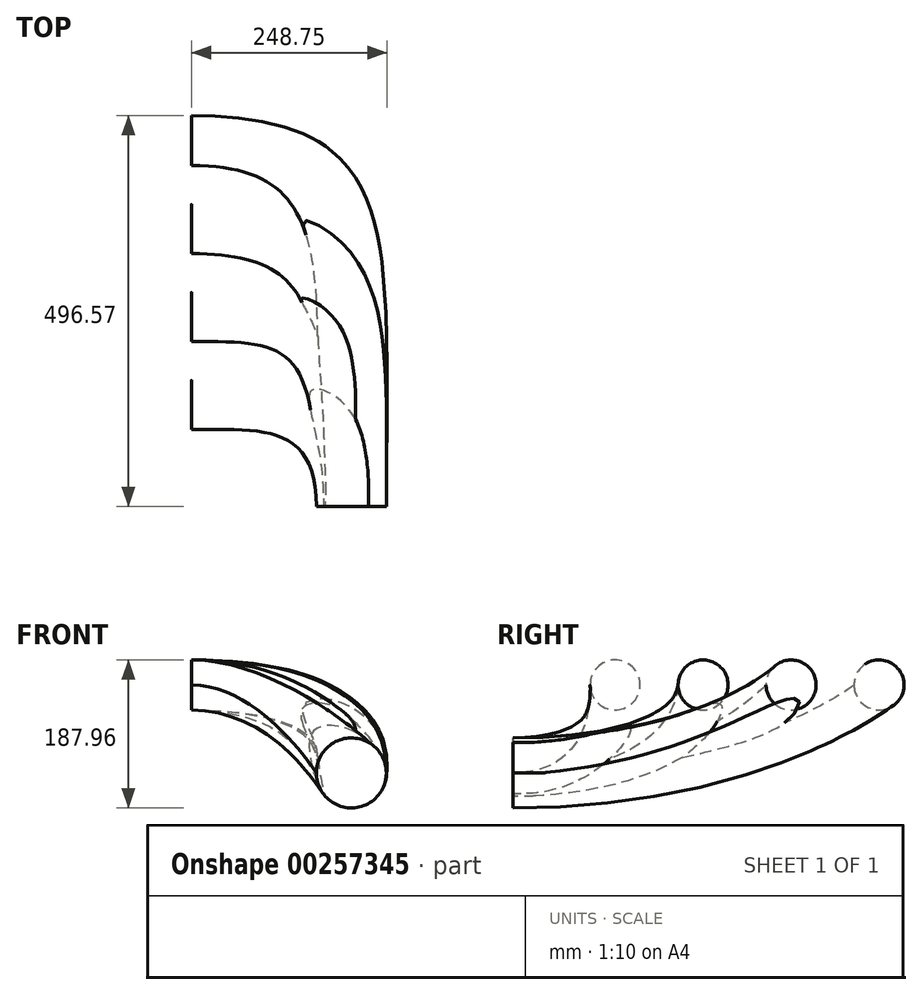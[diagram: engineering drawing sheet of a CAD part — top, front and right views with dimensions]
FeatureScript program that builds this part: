
annotation { "Feature Type Name" : "Feature", "Feature Type Description" : "" }
export const myFeature = defineFeature(function(context is Context, id is Id, definition is map)
    precondition{}
    {
        {
            var Q0;
            Q0=qCreatedBy(makeId("Right.planeOp"),FACE);
            cPlane(context, id + "F0", {"entities" : qUnion([Q0]), "cplaneType" : CPlaneType.OFFSET, "offset" : 203.2 * mm, "oppositeDirection" : true, "width" : 152.4 * mm, "height" : 152.4 * mm});
        }
        {
            var Q0;
            Q0=qCreatedBy(makeId("Top.planeOp"),FACE);
            cPlane(context, id + "F1", {"entities" : qUnion([Q0]), "cplaneType" : CPlaneType.OFFSET, "offset" : 111.76 * mm, "width" : 152.4 * mm, "height" : 152.4 * mm});
        }
        {
            var Q0;
            Q0=qCreatedBy(makeId("Front.planeOp"),FACE);
            var sketch = newSketch(context, id + "F2", { "sketchPlane" : qUnion([Q0])});
            skCircle(sketch, "E0", {"center": v(0, 0) * mm, "radius": 44.45 * mm});
            skSolve(sketch);
        }
        {
            var Q0;
            Q0=qCreatedBy(id+"F0.planeOp",FACE);
            var sketch = newSketch(context, id + "F3", { "sketchPlane" : qUnion([Q0])});
            skCircle(sketch, "E1", {"center": v(129.54, 111.76) * mm, "radius": 31.75 * mm});
            skCircle(sketch, "E2.1.0.0", {"center": v(241.3, 111.76) * mm, "radius": 31.75 * mm});
            skCircle(sketch, "E2.2.0.0", {"center": v(353.06, 111.76) * mm, "radius": 31.75 * mm});
            skCircle(sketch, "E2.3.0.0", {"center": v(464.82, 111.76) * mm, "radius": 31.75 * mm});
            skLineSegment(sketch, "E2.direction1", {"start": v(129.54, 111.76) * mm, "end": v(241.3, 111.76) * mm, "construction": true});
            skSolve(sketch);
        }
        {
            var Q0;
            Q0=qCreatedBy(id+"F1.planeOp",FACE);
            var sketch = newSketch(context, id + "F4", { "sketchPlane" : qUnion([Q0])});
            skLineSegment(sketch, "E3.0", {"start": v(-203.2, 161.3) * mm, "end": v(-203.2, 97.8) * mm, "construction": true});
            skLineSegment(sketch, "E4.0", {"start": v(-203.2, 273.05) * mm, "end": v(-203.2, 209.55) * mm, "construction": true});
            skLineSegment(sketch, "E5.0", {"start": v(-203.2, 384.81) * mm, "end": v(-203.2, 321.31) * mm, "construction": true});
            skLineSegment(sketch, "E6.0", {"start": v(-203.2, 496.57) * mm, "end": v(-203.2, 433.07) * mm, "construction": true});
            skLineSegment(sketch, "E7", {"start": v(-203.2, 97.8) * mm, "end": v(-177.8, 97.8) * mm, "construction": true});
            skLineSegment(sketch, "E8", {"start": v(-203.2, 209.55) * mm, "end": v(-177.8, 209.55) * mm, "construction": true});
            skLineSegment(sketch, "E9", {"start": v(-203.2, 321.31) * mm, "end": v(-177.8, 321.31) * mm, "construction": true});
            skLineSegment(sketch, "E10", {"start": v(-203.2, 433.07) * mm, "end": v(-177.8, 433.07) * mm, "construction": true});
            skSolve(sketch);
        }
        {
            var Q0;
            Q0=qCreatedBy(makeId("Top.planeOp"),FACE);
            var sketch = newSketch(context, id + "F5", { "sketchPlane" : qUnion([Q0])});
            skLineSegment(sketch, "E11.0", {"start": v(44.45, 0) * mm, "end": v(-44.45, 0) * mm, "construction": true});
            skLineSegment(sketch, "E12", {"start": v(-44.45, 0) * mm, "end": v(-44.45, 25.4) * mm, "construction": true});
            skSolve(sketch);
        }
        {
            var Q0;
            Q0=makeQuery(id+"F3.imprint","IMPRINT",FACE,{"disambiguationData":[TD([[makeQuery(id+"F3.imprint","IMPRINT",EDGE,{"derivedFrom":sQuery(id+"F3.wireOp",EDGE,"E1")}),1.0]])]});
            var Q1;
            Q1=makeQuery(id+"F2.imprint","IMPRINT",FACE,{"disambiguationData":[TD([[makeQuery(id+"F2.imprint","IMPRINT",EDGE,{"derivedFrom":sQuery(id+"F2.wireOp",EDGE,"E0")}),1.0]])]});
            var Q2;
            Q2=sQuery(id+"F4.wireOp",VERTEX,"E3.0.end");
            var Q3;
            Q3=sQuery(id+"F5.wireOp",VERTEX,"E12.start");
            loft(context, id + "F6", {"startCondition" : LoftEndDerivativeType.NORMAL_TO_PROFILE, "startMagnitude" : 1.6, "endCondition" : LoftEndDerivativeType.NORMAL_TO_PROFILE, "endMagnitude" : 2.9, "sheetProfilesArray" : [{ "sheetProfileEntities" : qUnion([Q0]) }, { "sheetProfileEntities" : qUnion([Q1]) }], "matchConnections" : true, "connections" : [{ "connectionEntities" : qUnion([Q2, Q3]), "connectionEdgeQueries" : qUnion([]), "connectionEdgeParameters" : [] }]});
        }
        {
            var Q1;
            Q1=makeQuery(id+"F3.imprint","IMPRINT",FACE,{"disambiguationData":[TD([[makeQuery(id+"F3.imprint","IMPRINT",EDGE,{"derivedFrom":sQuery(id+"F3.wireOp",EDGE,"E2.1.0.0")}),1.0]])]});
            var Q2;
            Q2=makeQuery(id+"F2.imprint","IMPRINT",FACE,{"disambiguationData":[TD([[makeQuery(id+"F2.imprint","IMPRINT",EDGE,{"derivedFrom":sQuery(id+"F2.wireOp",EDGE,"E0")}),1.0]])]});
            var Q3;
            Q3=sQuery(id+"F4.wireOp",VERTEX,"E8.start");
            var Q4;
            Q4=sQuery(id+"F5.wireOp",VERTEX,"E12.start");
            loft(context, id + "F7", {"operationType" : NewBodyOperationType.ADD, "startCondition" : LoftEndDerivativeType.NORMAL_TO_PROFILE, "startMagnitude" : 2.2, "endCondition" : LoftEndDerivativeType.NORMAL_TO_PROFILE, "endMagnitude" : 2.9, "sheetProfilesArray" : [{ "sheetProfileEntities" : qUnion([Q1]) }, { "sheetProfileEntities" : qUnion([Q2]) }], "matchConnections" : true, "connections" : [{ "connectionEntities" : qUnion([Q3, Q4]), "connectionEdgeQueries" : qUnion([]), "connectionEdgeParameters" : [] }]});
        }
        {
            var Q1;
            Q1=makeQuery(id+"F3.imprint","IMPRINT",FACE,{"disambiguationData":[TD([[makeQuery(id+"F3.imprint","IMPRINT",EDGE,{"derivedFrom":sQuery(id+"F3.wireOp",EDGE,"E2.2.0.0")}),1.0]])]});
            var Q2;
            Q2=makeQuery(id+"F2.imprint","IMPRINT",FACE,{"disambiguationData":[TD([[makeQuery(id+"F2.imprint","IMPRINT",EDGE,{"derivedFrom":sQuery(id+"F2.wireOp",EDGE,"E0")}),1.0]])]});
            var Q3;
            Q3=sQuery(id+"F4.wireOp",VERTEX,"E9.start");
            var Q4;
            Q4=sQuery(id+"F5.wireOp",VERTEX,"E12.start");
            loft(context, id + "F8", {"operationType" : NewBodyOperationType.ADD, "startCondition" : LoftEndDerivativeType.NORMAL_TO_PROFILE, "startMagnitude" : 3, "endCondition" : LoftEndDerivativeType.NORMAL_TO_PROFILE, "endMagnitude" : 2, "sheetProfilesArray" : [{ "sheetProfileEntities" : qUnion([Q1]) }, { "sheetProfileEntities" : qUnion([Q2]) }], "matchConnections" : true, "connections" : [{ "connectionEntities" : qUnion([Q3, Q4]), "connectionEdgeQueries" : qUnion([]), "connectionEdgeParameters" : [] }]});
        }
        {
            var Q1;
            Q1=makeQuery(id+"F3.imprint","IMPRINT",FACE,{"disambiguationData":[TD([[makeQuery(id+"F3.imprint","IMPRINT",EDGE,{"derivedFrom":sQuery(id+"F3.wireOp",EDGE,"E2.3.0.0")}),1.0]])]});
            var Q2;
            Q2=makeQuery(id+"F2.imprint","IMPRINT",FACE,{"disambiguationData":[TD([[makeQuery(id+"F2.imprint","IMPRINT",EDGE,{"derivedFrom":sQuery(id+"F2.wireOp",EDGE,"E0")}),1.0]])]});
            var Q3;
            Q3=sQuery(id+"F4.wireOp",VERTEX,"E6.0.end");
            var Q4;
            Q4=sQuery(id+"F5.wireOp",VERTEX,"E12.start");
            loft(context, id + "F9", {"operationType" : NewBodyOperationType.ADD, "startCondition" : LoftEndDerivativeType.NORMAL_TO_PROFILE, "startMagnitude" : 3, "endCondition" : LoftEndDerivativeType.NORMAL_TO_PROFILE, "endMagnitude" : 2, "sheetProfilesArray" : [{ "sheetProfileEntities" : qUnion([Q1]) }, { "sheetProfileEntities" : qUnion([Q2]) }], "matchConnections" : true, "connections" : [{ "connectionEntities" : qUnion([Q3, Q4]), "connectionEdgeQueries" : qUnion([]), "connectionEdgeParameters" : [] }]});
        }
    });
